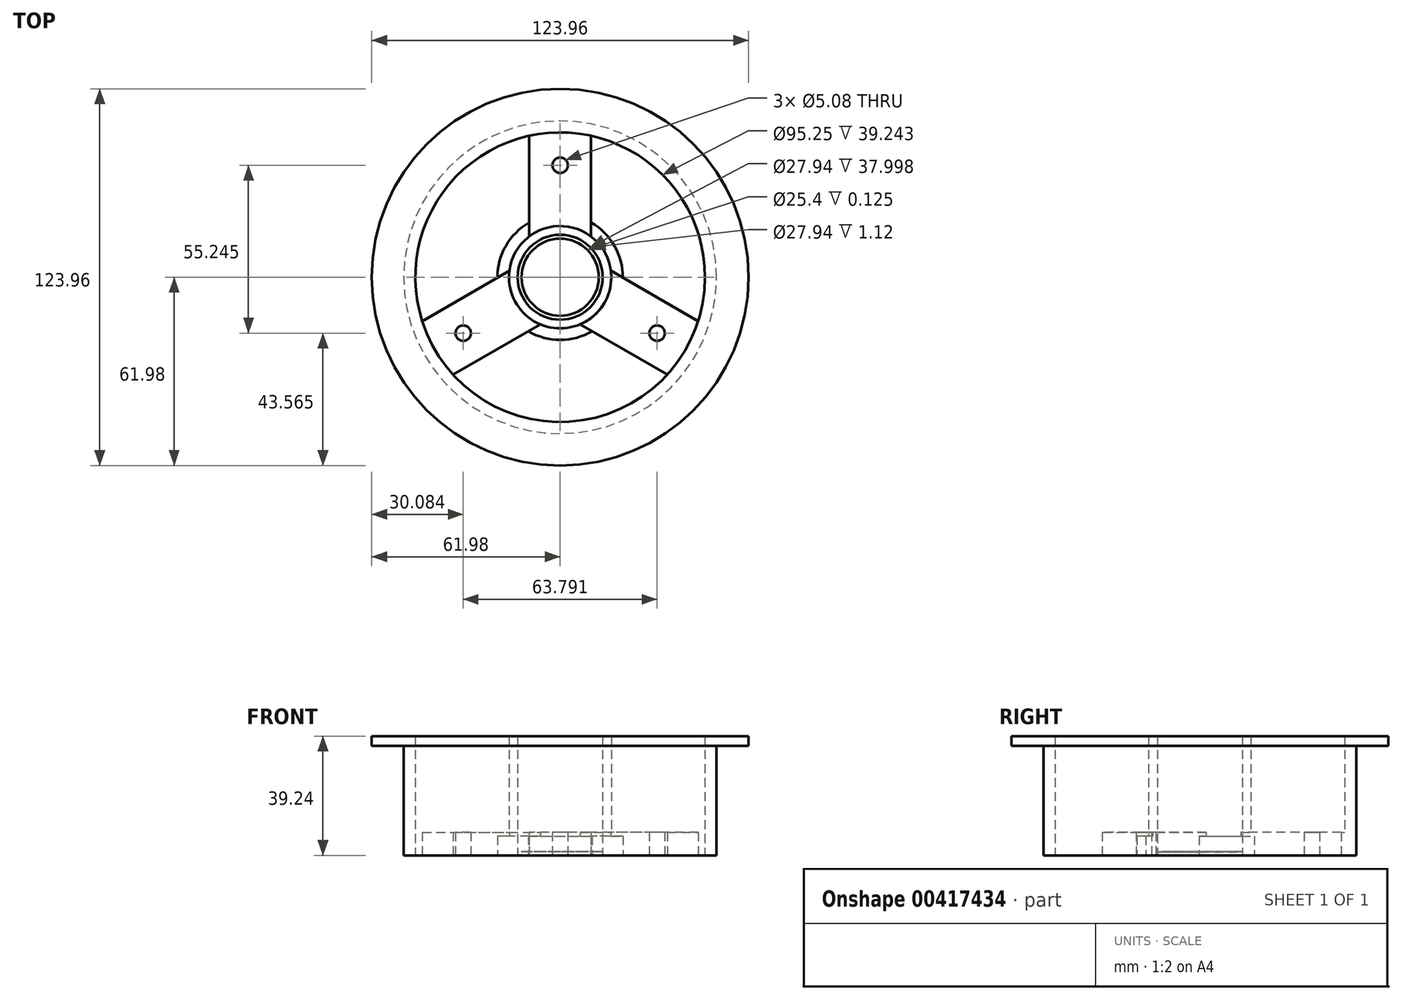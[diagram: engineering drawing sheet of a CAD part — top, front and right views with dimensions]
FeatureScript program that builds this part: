
annotation { "Feature Type Name" : "Feature", "Feature Type Description" : "" }
export const myFeature = defineFeature(function(context is Context, id is Id, definition is map)
    precondition{}
    {
        {
            var Q0;
            Q0=qCreatedBy(makeId("Top.planeOp"),FACE);
            var sketch = newSketch(context, id + "F0", { "sketchPlane" : qUnion([Q0])});
            skCircle(sketch, "E0", {"center": v(0, 0) * mm, "radius": 51.44 * mm});
            skCircle(sketch, "E1", {"center": v(0, 0) * mm, "radius": 20.64 * mm});
            skCircle(sketch, "E2", {"center": v(0, 0) * mm, "radius": 16.83 * mm});
            skCircle(sketch, "E3", {"center": v(0, 0) * mm, "radius": 13.97 * mm});
            skCircle(sketch, "E4", {"center": v(0, 0) * mm, "radius": 47.63 * mm});
            skLineSegment(sketch, "E5.bottom", {"start": v(-10.16, 50.42) * mm, "end": v(10.16, 50.42) * mm});
            skLineSegment(sketch, "E5.top", {"start": v(-10.16, 13.41) * mm, "end": v(-3.9, 13.41) * mm});
            skLineSegment(sketch, "E5.left", {"start": v(-10.16, 50.42) * mm, "end": v(-10.16, 13.41) * mm});
            skLineSegment(sketch, "E5.right", {"start": v(10.16, 50.42) * mm, "end": v(10.16, 13.41) * mm});
            skLineSegment(sketch, "E6.trimOffspring", {"start": v(3.9, 13.41) * mm, "end": v(10.16, 13.41) * mm});
            skCircle(sketch, "E7", {"center": v(0, 36.83) * mm, "radius": 2.54 * mm});
            skCircle(sketch, "E8", {"center": v(0, 0) * mm, "radius": 12.7 * mm});
            skLineSegment(sketch, "E9.bottom", {"start": v(-7.37, 25.92) * mm, "end": v(7.37, 25.92) * mm});
            skLineSegment(sketch, "E9.top", {"start": v(-7.37, 15.13) * mm, "end": v(7.37, 15.13) * mm});
            skLineSegment(sketch, "E9.left", {"start": v(-7.37, 25.92) * mm, "end": v(-7.37, 15.13) * mm});
            skLineSegment(sketch, "E9.right", {"start": v(7.37, 25.92) * mm, "end": v(7.37, 15.13) * mm});
            skLineSegment(sketch, "E10.1.0", {"start": v(-38.59, -34) * mm, "end": v(-48.75, -16.41) * mm});
            skLineSegment(sketch, "E10.1.1", {"start": v(-38.59, -34) * mm, "end": v(-6.54, -15.5) * mm});
            skLineSegment(sketch, "E10.1.2", {"start": v(-6.54, -15.5) * mm, "end": v(-9.67, -10.09) * mm});
            skLineSegment(sketch, "E10.1.3", {"start": v(-13.57, -3.33) * mm, "end": v(-16.7, 2.1) * mm});
            skLineSegment(sketch, "E10.1.4", {"start": v(-9.42, -13.94) * mm, "end": v(-16.79, -1.19) * mm});
            skLineSegment(sketch, "E10.1.5", {"start": v(-18.77, -19.34) * mm, "end": v(-9.42, -13.94) * mm});
            skLineSegment(sketch, "E10.1.6", {"start": v(-18.77, -19.34) * mm, "end": v(-26.13, -6.58) * mm});
            skLineSegment(sketch, "E10.1.7", {"start": v(-26.13, -6.58) * mm, "end": v(-16.79, -1.19) * mm});
            skCircle(sketch, "E10.1.8", {"center": v(-31.9, -18.41) * mm, "radius": 2.54 * mm});
            skLineSegment(sketch, "E10.1.9", {"start": v(-48.75, -16.41) * mm, "end": v(-16.7, 2.1) * mm});
            skLineSegment(sketch, "E10.2.0", {"start": v(48.75, -16.41) * mm, "end": v(38.59, -34) * mm});
            skLineSegment(sketch, "E10.2.1", {"start": v(48.75, -16.41) * mm, "end": v(16.7, 2.1) * mm});
            skLineSegment(sketch, "E10.2.2", {"start": v(16.7, 2.1) * mm, "end": v(13.57, -3.33) * mm});
            skLineSegment(sketch, "E10.2.3", {"start": v(9.67, -10.09) * mm, "end": v(6.54, -15.5) * mm});
            skLineSegment(sketch, "E10.2.4", {"start": v(16.79, -1.19) * mm, "end": v(9.42, -13.94) * mm});
            skLineSegment(sketch, "E10.2.5", {"start": v(26.13, -6.58) * mm, "end": v(16.79, -1.19) * mm});
            skLineSegment(sketch, "E10.2.6", {"start": v(26.13, -6.58) * mm, "end": v(18.77, -19.34) * mm});
            skLineSegment(sketch, "E10.2.7", {"start": v(18.77, -19.34) * mm, "end": v(9.42, -13.94) * mm});
            skCircle(sketch, "E10.2.8", {"center": v(31.9, -18.42) * mm, "radius": 2.54 * mm});
            skLineSegment(sketch, "E10.2.9", {"start": v(38.59, -34) * mm, "end": v(6.54, -15.5) * mm});
            skSolve(sketch);
        }
        {
            var Q0;
            {var subQ0=sQuery(id+"F0.wireOp",EDGE,"E5.left");var subQ5=sQuery(id+"F0.wireOp",EDGE,"E4");var subQ6=makeQuery(id+"F0.imprint","INTERSECT",VERTEX,{"derivedFrom":[subQ5,subQ0]});Q0=makeQuery(id+"F0.imprint","IMPRINT",FACE,{"disambiguationData":[TD([[makeQuery(id+"F0.imprint","IMPRINT",EDGE,{"disambiguationData":[TD([[subQ6,-1.0]])],"derivedFrom":subQ5}),-1.0]])]});}
            var Q1;
            {var subQ5=sQuery(id+"F0.wireOp",EDGE,"E5.bottom");Q1=makeQuery(id+"F0.imprint","IMPRINT",FACE,{"disambiguationData":[TD([[makeQuery(id+"F0.imprint","IMPRINT",EDGE,{"derivedFrom":subQ5}),-1.0]])]});}
            var Q2;
            {var subQ0=sQuery(id+"F0.wireOp",EDGE,"E5.bottom");Q2=makeQuery(id+"F0.imprint","IMPRINT",FACE,{"disambiguationData":[TD([[makeQuery(id+"F0.imprint","IMPRINT",EDGE,{"derivedFrom":subQ0}),1.0]])]});}
            var Q3;
            {var subQ0=sQuery(id+"F0.wireOp",EDGE,"E5.right");var subQ5=sQuery(id+"F0.wireOp",EDGE,"E4");var subQ6=makeQuery(id+"F0.imprint","INTERSECT",VERTEX,{"derivedFrom":[subQ5,subQ0]});Q3=makeQuery(id+"F0.imprint","IMPRINT",FACE,{"disambiguationData":[TD([[makeQuery(id+"F0.imprint","IMPRINT",EDGE,{"disambiguationData":[TD([[subQ6,1.0]])],"derivedFrom":subQ5}),-1.0]])]});}
            var Q4;
            {var subQ0=sQuery(id+"F0.wireOp",EDGE,"E10.2.0");Q4=makeQuery(id+"F0.imprint","IMPRINT",FACE,{"disambiguationData":[TD([[makeQuery(id+"F0.imprint","IMPRINT",EDGE,{"derivedFrom":subQ0}),1.0]])]});}
            var Q5;
            {var subQ5=sQuery(id+"F0.wireOp",EDGE,"E10.2.0");Q5=makeQuery(id+"F0.imprint","IMPRINT",FACE,{"disambiguationData":[TD([[makeQuery(id+"F0.imprint","IMPRINT",EDGE,{"derivedFrom":subQ5}),-1.0]])]});}
            var Q6;
            {var subQ0=sQuery(id+"F0.wireOp",EDGE,"E10.1.1");var subQ5=sQuery(id+"F0.wireOp",EDGE,"E4");var subQ7=makeQuery(id+"F0.imprint","INTERSECT",VERTEX,{"derivedFrom":[subQ5,subQ0]});Q6=makeQuery(id+"F0.imprint","IMPRINT",FACE,{"disambiguationData":[TD([[makeQuery(id+"F0.imprint","IMPRINT",EDGE,{"disambiguationData":[TD([[subQ7,-1.0]])],"derivedFrom":subQ5}),-1.0]])]});}
            var Q7;
            {var subQ0=sQuery(id+"F0.wireOp",EDGE,"E10.1.0");Q7=makeQuery(id+"F0.imprint","IMPRINT",FACE,{"disambiguationData":[TD([[makeQuery(id+"F0.imprint","IMPRINT",EDGE,{"derivedFrom":subQ0}),1.0]])]});}
            var Q8;
            {var subQ5=sQuery(id+"F0.wireOp",EDGE,"E10.1.0");Q8=makeQuery(id+"F0.imprint","IMPRINT",FACE,{"disambiguationData":[TD([[makeQuery(id+"F0.imprint","IMPRINT",EDGE,{"derivedFrom":subQ5}),-1.0]])]});}
            extrude(context, id + "F1", {"entities" : qUnion([Q0, Q1, Q2, Q3, Q4, Q5, Q6, Q7, Q8]), "depth" : 36.07 * mm});
        }
        {
            var Q0;
            {var subQ0=sQuery(id+"F0.wireOp",EDGE,"E5.left");var subQ1=sQuery(id+"F0.wireOp",EDGE,"E1");var subQ2=makeQuery(id+"F0.imprint","INTERSECT",VERTEX,{"derivedFrom":[subQ1,subQ0]});Q0=makeQuery(id+"F0.imprint","IMPRINT",FACE,{"disambiguationData":[TD([[makeQuery(id+"F0.imprint","IMPRINT",EDGE,{"disambiguationData":[TD([[subQ2,-1.0]])],"derivedFrom":subQ1}),1.0]])]});}
            var Q1;
            {var subQ0=sQuery(id+"F0.wireOp",EDGE,"E9.right");var subQ1=sQuery(id+"F0.wireOp",EDGE,"E1");var subQ2=makeQuery(id+"F0.imprint","INTERSECT",VERTEX,{"derivedFrom":[subQ1,subQ0]});Q1=makeQuery(id+"F0.imprint","IMPRINT",FACE,{"disambiguationData":[TD([[makeQuery(id+"F0.imprint","IMPRINT",EDGE,{"disambiguationData":[TD([[subQ2,-1.0]])],"derivedFrom":subQ1}),1.0]])]});}
            var Q2;
            {var subQ0=sQuery(id+"F0.wireOp",EDGE,"E9.right");var subQ1=sQuery(id+"F0.wireOp",EDGE,"E1");var subQ2=makeQuery(id+"F0.imprint","INTERSECT",VERTEX,{"derivedFrom":[subQ1,subQ0]});Q2=makeQuery(id+"F0.imprint","IMPRINT",FACE,{"disambiguationData":[TD([[makeQuery(id+"F0.imprint","IMPRINT",EDGE,{"disambiguationData":[TD([[subQ2,1.0]])],"derivedFrom":subQ1}),1.0]])]});}
            var Q3;
            {var subQ0=sQuery(id+"F0.wireOp",EDGE,"E5.right");var subQ1=sQuery(id+"F0.wireOp",EDGE,"E1");var subQ2=makeQuery(id+"F0.imprint","INTERSECT",VERTEX,{"derivedFrom":[subQ1,subQ0]});Q3=makeQuery(id+"F0.imprint","IMPRINT",FACE,{"disambiguationData":[TD([[makeQuery(id+"F0.imprint","IMPRINT",EDGE,{"disambiguationData":[TD([[subQ2,1.0]])],"derivedFrom":subQ1}),1.0]])]});}
            var Q4;
            {var subQ0=sQuery(id+"F0.wireOp",EDGE,"E10.2.7");var subQ1=sQuery(id+"F0.wireOp",EDGE,"E1");var subQ2=makeQuery(id+"F0.imprint","INTERSECT",VERTEX,{"derivedFrom":[subQ1,subQ0]});Q4=makeQuery(id+"F0.imprint","IMPRINT",FACE,{"disambiguationData":[TD([[makeQuery(id+"F0.imprint","IMPRINT",EDGE,{"disambiguationData":[TD([[subQ2,-1.0]])],"derivedFrom":subQ1}),1.0]])]});}
            var Q5;
            {var subQ0=sQuery(id+"F0.wireOp",EDGE,"E9.left");var subQ1=sQuery(id+"F0.wireOp",EDGE,"E1");var subQ2=makeQuery(id+"F0.imprint","INTERSECT",VERTEX,{"derivedFrom":[subQ1,subQ0]});Q5=makeQuery(id+"F0.imprint","IMPRINT",FACE,{"disambiguationData":[TD([[makeQuery(id+"F0.imprint","IMPRINT",EDGE,{"disambiguationData":[TD([[subQ2,-1.0]])],"derivedFrom":subQ1}),1.0]])]});}
            var Q6;
            {var subQ0=sQuery(id+"F0.wireOp",EDGE,"E10.2.5");var subQ1=sQuery(id+"F0.wireOp",EDGE,"E1");var subQ2=makeQuery(id+"F0.imprint","INTERSECT",VERTEX,{"derivedFrom":[subQ1,subQ0]});Q6=makeQuery(id+"F0.imprint","IMPRINT",FACE,{"disambiguationData":[TD([[makeQuery(id+"F0.imprint","IMPRINT",EDGE,{"disambiguationData":[TD([[subQ2,-1.0]])],"derivedFrom":subQ1}),1.0]])]});}
            var Q7;
            {var subQ0=sQuery(id+"F0.wireOp",EDGE,"E10.2.9");var subQ1=sQuery(id+"F0.wireOp",EDGE,"E1");var subQ2=makeQuery(id+"F0.imprint","INTERSECT",VERTEX,{"derivedFrom":[subQ1,subQ0]});Q7=makeQuery(id+"F0.imprint","IMPRINT",FACE,{"disambiguationData":[TD([[makeQuery(id+"F0.imprint","IMPRINT",EDGE,{"disambiguationData":[TD([[subQ2,-1.0]])],"derivedFrom":subQ1}),1.0]])]});}
            var Q8;
            {var subQ0=sQuery(id+"F0.wireOp",EDGE,"E10.1.1");var subQ1=sQuery(id+"F0.wireOp",EDGE,"E1");var subQ2=makeQuery(id+"F0.imprint","INTERSECT",VERTEX,{"derivedFrom":[subQ1,subQ0]});Q8=makeQuery(id+"F0.imprint","IMPRINT",FACE,{"disambiguationData":[TD([[makeQuery(id+"F0.imprint","IMPRINT",EDGE,{"disambiguationData":[TD([[subQ2,-1.0]])],"derivedFrom":subQ1}),1.0]])]});}
            var Q9;
            {var subQ0=sQuery(id+"F0.wireOp",EDGE,"E10.1.5");var subQ1=sQuery(id+"F0.wireOp",EDGE,"E1");var subQ2=makeQuery(id+"F0.imprint","INTERSECT",VERTEX,{"derivedFrom":[subQ1,subQ0]});Q9=makeQuery(id+"F0.imprint","IMPRINT",FACE,{"disambiguationData":[TD([[makeQuery(id+"F0.imprint","IMPRINT",EDGE,{"disambiguationData":[TD([[subQ2,-1.0]])],"derivedFrom":subQ1}),1.0]])]});}
            var Q10;
            {var subQ0=sQuery(id+"F0.wireOp",EDGE,"E10.1.7");var subQ1=sQuery(id+"F0.wireOp",EDGE,"E1");var subQ2=makeQuery(id+"F0.imprint","INTERSECT",VERTEX,{"derivedFrom":[subQ1,subQ0]});Q10=makeQuery(id+"F0.imprint","IMPRINT",FACE,{"disambiguationData":[TD([[makeQuery(id+"F0.imprint","IMPRINT",EDGE,{"disambiguationData":[TD([[subQ2,-1.0]])],"derivedFrom":subQ1}),1.0]])]});}
            var Q11;
            {var subQ0=sQuery(id+"F0.wireOp",EDGE,"E10.1.9");var subQ1=sQuery(id+"F0.wireOp",EDGE,"E1");var subQ2=makeQuery(id+"F0.imprint","INTERSECT",VERTEX,{"derivedFrom":[subQ1,subQ0]});Q11=makeQuery(id+"F0.imprint","IMPRINT",FACE,{"disambiguationData":[TD([[makeQuery(id+"F0.imprint","IMPRINT",EDGE,{"disambiguationData":[TD([[subQ2,-1.0]])],"derivedFrom":subQ1}),1.0]])]});}
            extrude(context, id + "F2", {"entities" : qUnion([Q0, Q1, Q2, Q3, Q4, Q5, Q6, Q7, Q8, Q9, Q10, Q11]), "depth" : 6.35 * mm});
        }
        {
            var Q0;
            {var subQ12=sQuery(id+"F0.wireOp",EDGE,"E10.1.6");Q0=makeQuery(id+"F0.imprint","IMPRINT",FACE,{"disambiguationData":[TD([[makeQuery(id+"F0.imprint","IMPRINT",EDGE,{"derivedFrom":subQ12}),1.0]])]});}
            var Q1;
            {var subQ5=sQuery(id+"F0.wireOp",EDGE,"E10.1.6");Q1=makeQuery(id+"F0.imprint","IMPRINT",FACE,{"disambiguationData":[TD([[makeQuery(id+"F0.imprint","IMPRINT",EDGE,{"derivedFrom":subQ5}),-1.0]])]});}
            var Q2;
            {var subQ5=sQuery(id+"F0.wireOp",EDGE,"E9.bottom");Q2=makeQuery(id+"F0.imprint","IMPRINT",FACE,{"disambiguationData":[TD([[makeQuery(id+"F0.imprint","IMPRINT",EDGE,{"derivedFrom":subQ5}),-1.0]])]});}
            var Q3;
            Q3=makeQuery(id+"F0.imprint","IMPRINT",FACE,{"disambiguationData":[TD([[makeQuery(id+"F0.imprint","IMPRINT",EDGE,{"derivedFrom":sQuery(id+"F0.wireOp",EDGE,"E7")}),-1.0]])]});
            var Q4;
            {var subQ5=sQuery(id+"F0.wireOp",EDGE,"E10.2.6");Q4=makeQuery(id+"F0.imprint","IMPRINT",FACE,{"disambiguationData":[TD([[makeQuery(id+"F0.imprint","IMPRINT",EDGE,{"derivedFrom":subQ5}),-1.0]])]});}
            var Q5;
            {var subQ7=sQuery(id+"F0.wireOp",EDGE,"E10.2.6");Q5=makeQuery(id+"F0.imprint","IMPRINT",FACE,{"disambiguationData":[TD([[makeQuery(id+"F0.imprint","IMPRINT",EDGE,{"derivedFrom":subQ7}),1.0]])]});}
            var Q6;
            {var subQ0=sQuery(id+"F0.wireOp",EDGE,"E10.1.7");var subQ1=sQuery(id+"F0.wireOp",EDGE,"E1");var subQ2=makeQuery(id+"F0.imprint","INTERSECT",VERTEX,{"derivedFrom":[subQ1,subQ0]});Q6=makeQuery(id+"F0.imprint","IMPRINT",FACE,{"disambiguationData":[TD([[makeQuery(id+"F0.imprint","IMPRINT",EDGE,{"disambiguationData":[TD([[subQ2,-1.0]])],"derivedFrom":subQ1}),1.0]])]});}
            var Q7;
            {var subQ0=sQuery(id+"F0.wireOp",EDGE,"E10.1.9");var subQ1=sQuery(id+"F0.wireOp",EDGE,"E1");var subQ2=makeQuery(id+"F0.imprint","INTERSECT",VERTEX,{"derivedFrom":[subQ1,subQ0]});Q7=makeQuery(id+"F0.imprint","IMPRINT",FACE,{"disambiguationData":[TD([[makeQuery(id+"F0.imprint","IMPRINT",EDGE,{"disambiguationData":[TD([[subQ2,-1.0]])],"derivedFrom":subQ1}),1.0]])]});}
            var Q8;
            {var subQ0=sQuery(id+"F0.wireOp",EDGE,"E10.1.5");var subQ1=sQuery(id+"F0.wireOp",EDGE,"E1");var subQ2=makeQuery(id+"F0.imprint","INTERSECT",VERTEX,{"derivedFrom":[subQ1,subQ0]});Q8=makeQuery(id+"F0.imprint","IMPRINT",FACE,{"disambiguationData":[TD([[makeQuery(id+"F0.imprint","IMPRINT",EDGE,{"disambiguationData":[TD([[subQ2,-1.0]])],"derivedFrom":subQ1}),1.0]])]});}
            var Q9;
            {var subQ0=sQuery(id+"F0.wireOp",EDGE,"E10.2.7");var subQ1=sQuery(id+"F0.wireOp",EDGE,"E1");var subQ2=makeQuery(id+"F0.imprint","INTERSECT",VERTEX,{"derivedFrom":[subQ1,subQ0]});Q9=makeQuery(id+"F0.imprint","IMPRINT",FACE,{"disambiguationData":[TD([[makeQuery(id+"F0.imprint","IMPRINT",EDGE,{"disambiguationData":[TD([[subQ2,-1.0]])],"derivedFrom":subQ1}),1.0]])]});}
            var Q10;
            {var subQ0=sQuery(id+"F0.wireOp",EDGE,"E10.2.9");var subQ1=sQuery(id+"F0.wireOp",EDGE,"E1");var subQ2=makeQuery(id+"F0.imprint","INTERSECT",VERTEX,{"derivedFrom":[subQ1,subQ0]});Q10=makeQuery(id+"F0.imprint","IMPRINT",FACE,{"disambiguationData":[TD([[makeQuery(id+"F0.imprint","IMPRINT",EDGE,{"disambiguationData":[TD([[subQ2,-1.0]])],"derivedFrom":subQ1}),1.0]])]});}
            var Q11;
            {var subQ0=sQuery(id+"F0.wireOp",EDGE,"E10.2.5");var subQ1=sQuery(id+"F0.wireOp",EDGE,"E1");var subQ2=makeQuery(id+"F0.imprint","INTERSECT",VERTEX,{"derivedFrom":[subQ1,subQ0]});Q11=makeQuery(id+"F0.imprint","IMPRINT",FACE,{"disambiguationData":[TD([[makeQuery(id+"F0.imprint","IMPRINT",EDGE,{"disambiguationData":[TD([[subQ2,-1.0]])],"derivedFrom":subQ1}),1.0]])]});}
            var Q12;
            {var subQ0=sQuery(id+"F0.wireOp",EDGE,"E9.left");var subQ1=sQuery(id+"F0.wireOp",EDGE,"E1");var subQ2=makeQuery(id+"F0.imprint","INTERSECT",VERTEX,{"derivedFrom":[subQ1,subQ0]});Q12=makeQuery(id+"F0.imprint","IMPRINT",FACE,{"disambiguationData":[TD([[makeQuery(id+"F0.imprint","IMPRINT",EDGE,{"disambiguationData":[TD([[subQ2,-1.0]])],"derivedFrom":subQ1}),1.0]])]});}
            var Q13;
            {var subQ0=sQuery(id+"F0.wireOp",EDGE,"E9.right");var subQ1=sQuery(id+"F0.wireOp",EDGE,"E1");var subQ2=makeQuery(id+"F0.imprint","INTERSECT",VERTEX,{"derivedFrom":[subQ1,subQ0]});Q13=makeQuery(id+"F0.imprint","IMPRINT",FACE,{"disambiguationData":[TD([[makeQuery(id+"F0.imprint","IMPRINT",EDGE,{"disambiguationData":[TD([[subQ2,-1.0]])],"derivedFrom":subQ1}),1.0]])]});}
            var Q14;
            {var subQ0=sQuery(id+"F0.wireOp",EDGE,"E9.right");var subQ1=sQuery(id+"F0.wireOp",EDGE,"E1");var subQ2=makeQuery(id+"F0.imprint","INTERSECT",VERTEX,{"derivedFrom":[subQ1,subQ0]});Q14=makeQuery(id+"F0.imprint","IMPRINT",FACE,{"disambiguationData":[TD([[makeQuery(id+"F0.imprint","IMPRINT",EDGE,{"disambiguationData":[TD([[subQ2,1.0]])],"derivedFrom":subQ1}),1.0]])]});}
            extrude(context, id + "F3", {"entities" : qUnion([Q0, Q1, Q2, Q3, Q4, Q5, Q6, Q7, Q8, Q9, Q10, Q11, Q12, Q13, Q14]), "operationType" : NewBodyOperationType.ADD, "depth" : 7.62 * mm});
        }
        {
            var Q0;
            {var subQ0=sQuery(id+"F0.wireOp",EDGE,"E5.top");Q0=makeQuery(id+"F0.imprint","IMPRINT",FACE,{"disambiguationData":[TD([[makeQuery(id+"F0.imprint","IMPRINT",EDGE,{"derivedFrom":subQ0}),1.0]])]});}
            var Q1;
            {var subQ0=sQuery(id+"F0.wireOp",EDGE,"E9.top");Q1=makeQuery(id+"F0.imprint","IMPRINT",FACE,{"disambiguationData":[TD([[makeQuery(id+"F0.imprint","IMPRINT",EDGE,{"derivedFrom":subQ0}),1.0]])]});}
            var Q2;
            {var subQ0=sQuery(id+"F0.wireOp",EDGE,"E6.trimOffspring");Q2=makeQuery(id+"F0.imprint","IMPRINT",FACE,{"disambiguationData":[TD([[makeQuery(id+"F0.imprint","IMPRINT",EDGE,{"derivedFrom":subQ0}),-1.0]])]});}
            var Q3;
            {var subQ0=sQuery(id+"F0.wireOp",EDGE,"E10.2.4");Q3=makeQuery(id+"F0.imprint","IMPRINT",FACE,{"disambiguationData":[TD([[makeQuery(id+"F0.imprint","IMPRINT",EDGE,{"derivedFrom":subQ0}),1.0]])]});}
            var Q4;
            {var subQ0=sQuery(id+"F0.wireOp",EDGE,"E10.2.2");Q4=makeQuery(id+"F0.imprint","IMPRINT",FACE,{"disambiguationData":[TD([[makeQuery(id+"F0.imprint","IMPRINT",EDGE,{"derivedFrom":subQ0}),1.0]])]});}
            var Q5;
            {var subQ0=sQuery(id+"F0.wireOp",EDGE,"E10.1.2");Q5=makeQuery(id+"F0.imprint","IMPRINT",FACE,{"disambiguationData":[TD([[makeQuery(id+"F0.imprint","IMPRINT",EDGE,{"derivedFrom":subQ0}),-1.0]])]});}
            var Q6;
            {var subQ0=sQuery(id+"F0.wireOp",EDGE,"E10.1.2");Q6=makeQuery(id+"F0.imprint","IMPRINT",FACE,{"disambiguationData":[TD([[makeQuery(id+"F0.imprint","IMPRINT",EDGE,{"derivedFrom":subQ0}),1.0]])]});}
            var Q7;
            {var subQ0=sQuery(id+"F0.wireOp",EDGE,"E10.1.4");Q7=makeQuery(id+"F0.imprint","IMPRINT",FACE,{"disambiguationData":[TD([[makeQuery(id+"F0.imprint","IMPRINT",EDGE,{"derivedFrom":subQ0}),1.0]])]});}
            var Q8;
            {var subQ0=sQuery(id+"F0.wireOp",EDGE,"E5.top");Q8=makeQuery(id+"F0.imprint","IMPRINT",FACE,{"disambiguationData":[TD([[makeQuery(id+"F0.imprint","IMPRINT",EDGE,{"derivedFrom":subQ0}),-1.0]])]});}
            extrude(context, id + "F4", {"entities" : qUnion([Q0, Q1, Q2, Q3, Q4, Q5, Q6, Q7, Q8]), "operationType" : NewBodyOperationType.ADD, "depth" : 39.24 * mm});
        }
        {
            var Q0;
            Q0=makeQuery(id+"F0.imprint","IMPRINT",FACE,{"disambiguationData":[TD([[makeQuery(id+"F0.imprint","IMPRINT",EDGE,{"derivedFrom":sQuery(id+"F0.wireOp",EDGE,"E8")}),-1.0]])]});
            extrude(context, id + "F5", {"entities" : qUnion([Q0]), "operationType" : NewBodyOperationType.ADD, "depth" : ((1.42 + 0.12) - .3) * mm});
        }
        {
            var Q0;
            Q0=makeQuery(id+"F0.imprint","IMPRINT",FACE,{"disambiguationData":[TD([[makeQuery(id+"F0.imprint","IMPRINT",EDGE,{"derivedFrom":sQuery(id+"F0.wireOp",EDGE,"E8")}),-1.0]])]});
            extrude(context, id + "F6", {"entities" : qUnion([Q0]), "operationType" : NewBodyOperationType.REMOVE, "depth" : ((1.42 + 0.12) - 0.42) * mm});
        }
        {
            var Q0;
            Q0=makeQuery(id+"F1.opExtrude","CAP_FACE",FACE,{"disambiguationData":[OSD([sQuery(id+"F0.wireOp",EDGE,"E0"),sQuery(id+"F0.wireOp",EDGE,"E4")])],"isStart":false});
            var sketch = newSketch(context, id + "F7", { "sketchPlane" : qUnion([Q0])});
            skCircle(sketch, "E11", {"center": v(0, 0) * mm, "radius": 47.63 * mm});
            skCircle(sketch, "E12", {"center": v(0, 0) * mm, "radius": 61.98 * mm});
            skSolve(sketch);
        }
        {
            var Q0;
            Q0=makeQuery(id+"F7.imprint","IMPRINT",FACE,{"disambiguationData":[TD([[makeQuery(id+"F7.imprint","IMPRINT",EDGE,{"derivedFrom":sQuery(id+"F7.wireOp",EDGE,"E12")}),1.0]])]});
            var Q1;
            Q1=makeQuery(id+"F7.imprint","IMPRINT",FACE,{"disambiguationData":[TD([[makeQuery(id+"F7.imprint","IMPRINT",EDGE,{"derivedFrom":sQuery(id+"F7.wireOp",EDGE,"E11")}),-1.0]])]});
            extrude(context, id + "F8", {"entities" : qUnion([Q0, Q1]), "operationType" : NewBodyOperationType.ADD, "depth" : 3.17 * mm});
        }
    });
